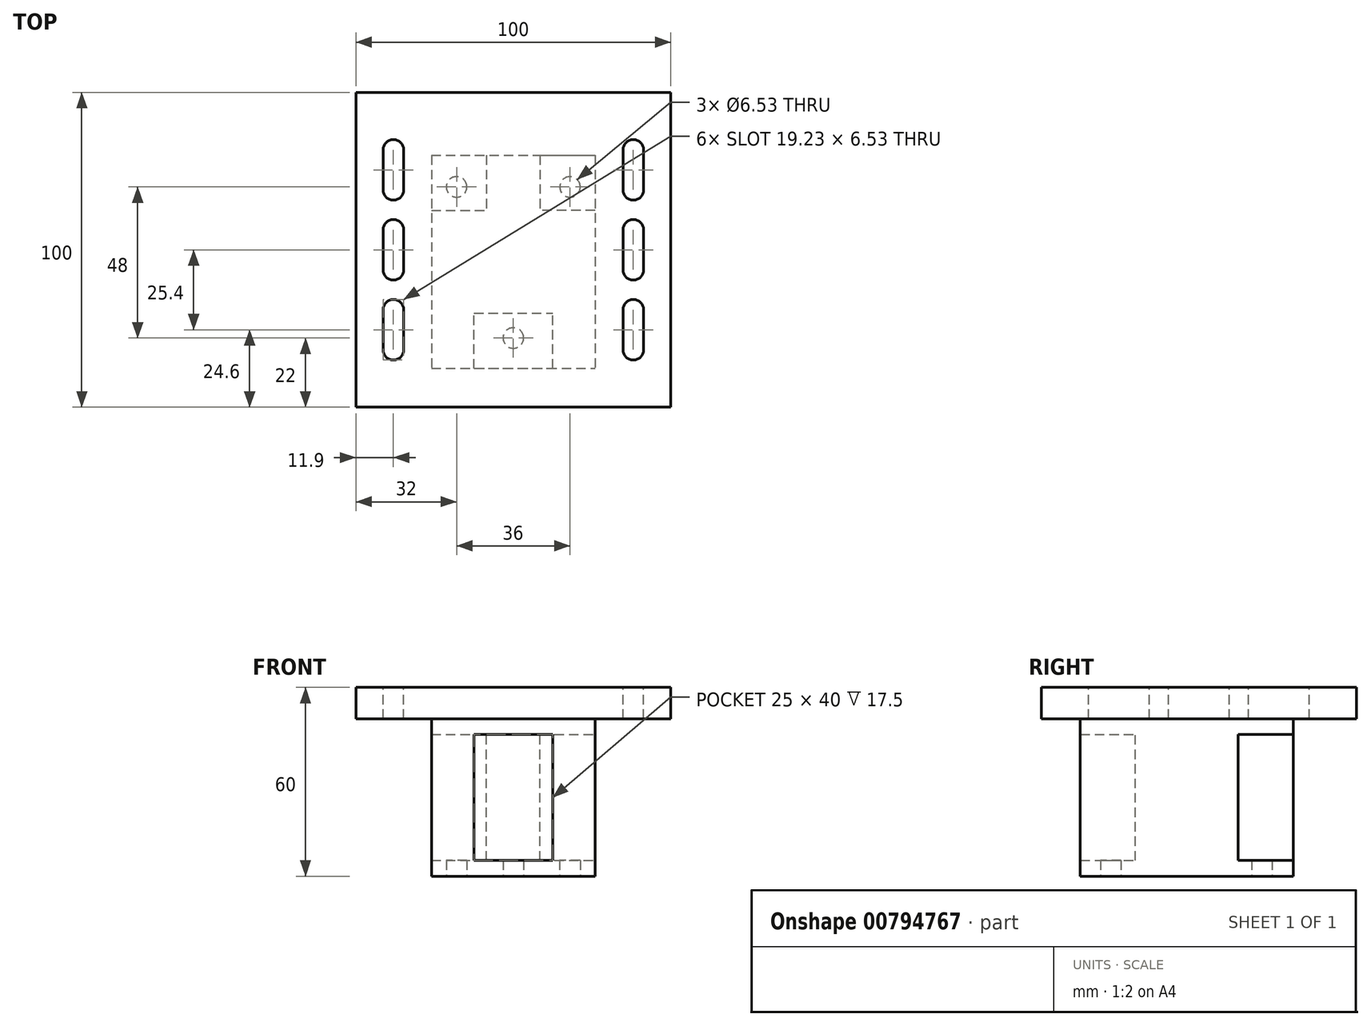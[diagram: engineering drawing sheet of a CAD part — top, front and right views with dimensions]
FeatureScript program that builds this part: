
annotation { "Feature Type Name" : "Feature", "Feature Type Description" : "" }
export const myFeature = defineFeature(function(context is Context, id is Id, definition is map)
    precondition{}
    {
        {
            var Q0;
            Q0=qCreatedBy(makeId("Top.planeOp"),FACE);
            var sketch = newSketch(context, id + "F0", { "sketchPlane" : qUnion([Q0])});
            skLineSegment(sketch, "E0.bottom", {"start": v(-26, 30) * mm, "end": v(26, 30) * mm});
            skLineSegment(sketch, "E0.top", {"start": v(-26, -37.66) * mm, "end": v(26, -37.66) * mm});
            skLineSegment(sketch, "E0.left", {"start": v(-26, 30) * mm, "end": v(-26, -37.66) * mm});
            skLineSegment(sketch, "E0.right", {"start": v(26, 30) * mm, "end": v(26, -37.66) * mm});
            skSolve(sketch);
        }
        {
            var Q0;
            Q0=makeQuery(id+"F0.imprint","IMPRINT",FACE,{"disambiguationData":[TD([[makeQuery(id+"F0.imprint","IMPRINT",EDGE,{"derivedFrom":sQuery(id+"F0.wireOp",EDGE,"E0.bottom")}),-1.0]])]});
            var sketch = newSketch(context, id + "F1", { "sketchPlane" : qUnion([Q0])});
            skCircle(sketch, "E1", {"center": v(-18, 20) * mm, "radius": 3.27 * mm});
            skCircle(sketch, "E2", {"center": v(18, 20) * mm, "radius": 3.27 * mm});
            skCircle(sketch, "E3", {"center": v(0, -28) * mm, "radius": 3.27 * mm});
            skSolve(sketch);
        }
        {
            var Q0;
            Q0=qSketchRegion(id+"F0",true);
            extrude(context, id + "F2", {"entities" : qUnion([Q0]), "depth" : 5 * mm, "offsetDistance" : 25 * mm});
        }
        {
            var Q0;
            Q0=qSketchRegion(id+"F1",true);
            extrude(context, id + "F3", {"entities" : qUnion([Q0]), "operationType" : NewBodyOperationType.REMOVE, "oppositeDirection" : true, "depth" : -5 * mm, "offsetDistance" : 25 * mm});
        }
        {
            var Q0;
            Q0=makeQuery(id+"F2.opExtrude","CAP_FACE",FACE,{"disambiguationData":[OSD([sQuery(id+"F0.wireOp",EDGE,"E0.bottom"),sQuery(id+"F0.wireOp",EDGE,"E0.top"),sQuery(id+"F0.wireOp",EDGE,"E0.left"),sQuery(id+"F0.wireOp",EDGE,"E0.right")])],"isStart":false});
            var sketch = newSketch(context, id + "F4", { "sketchPlane" : qUnion([Q0])});
            skLineSegment(sketch, "E4.bottom", {"start": v(-26, 30) * mm, "end": v(26, 30) * mm});
            skLineSegment(sketch, "E4.top", {"start": v(-26, -37.66) * mm, "end": v(26, -37.66) * mm});
            skLineSegment(sketch, "E4.left", {"start": v(-26, 30) * mm, "end": v(-26, -37.66) * mm});
            skLineSegment(sketch, "E4.right", {"start": v(26, 30) * mm, "end": v(26, -37.66) * mm});
            skSolve(sketch);
        }
        {
            var Q0;
            Q0=qSketchRegion(id+"F4",true);
            extrude(context, id + "F5", {"entities" : qUnion([Q0]), "operationType" : NewBodyOperationType.ADD, "depth" : 30 * mm, "offsetDistance" : 25 * mm});
        }
        {
            var Q0;
            Q0=makeQuery(id+"F5.opExtrude","CAP_FACE",FACE,{"disambiguationData":[OSD([sQuery(id+"F4.wireOp",EDGE,"E4.bottom"),sQuery(id+"F4.wireOp",EDGE,"E4.top"),sQuery(id+"F4.wireOp",EDGE,"E4.left"),sQuery(id+"F4.wireOp",EDGE,"E4.right")])],"isStart":false});
            var sketch = newSketch(context, id + "F6", { "sketchPlane" : qUnion([Q0])});
            skLineSegment(sketch, "E5.bottom", {"start": v(-26, 30) * mm, "end": v(-8.5, 30) * mm});
            skLineSegment(sketch, "E5.top", {"start": v(-26, 12.5) * mm, "end": v(-8.5, 12.5) * mm});
            skLineSegment(sketch, "E5.left", {"start": v(-26, 30) * mm, "end": v(-26, 12.5) * mm});
            skLineSegment(sketch, "E5.right", {"start": v(-8.5, 30) * mm, "end": v(-8.5, 12.5) * mm});
            skLineSegment(sketch, "E6.bottom", {"start": v(26, 30) * mm, "end": v(8.5, 30) * mm});
            skLineSegment(sketch, "E6.top", {"start": v(26, 12.5) * mm, "end": v(8.5, 12.5) * mm});
            skLineSegment(sketch, "E6.left", {"start": v(26, 30) * mm, "end": v(26, 12.5) * mm});
            skLineSegment(sketch, "E6.right", {"start": v(8.5, 30) * mm, "end": v(8.5, 12.5) * mm});
            skLineSegment(sketch, "E7.bottom", {"start": v(-12.5, -37.66) * mm, "end": v(12.5, -37.66) * mm});
            skLineSegment(sketch, "E7.top", {"start": v(-12.5, -20.16) * mm, "end": v(12.5, -20.16) * mm});
            skLineSegment(sketch, "E7.left", {"start": v(-12.5, -37.66) * mm, "end": v(-12.5, -20.16) * mm});
            skLineSegment(sketch, "E7.right", {"start": v(12.5, -37.66) * mm, "end": v(12.5, -20.16) * mm});
            skSolve(sketch);
        }
        {
            var Q0;
            Q0=makeQuery(id+"F5.opExtrude","CAP_FACE",FACE,{"disambiguationData":[OSD([sQuery(id+"F4.wireOp",EDGE,"E4.bottom"),sQuery(id+"F4.wireOp",EDGE,"E4.top"),sQuery(id+"F4.wireOp",EDGE,"E4.left"),sQuery(id+"F4.wireOp",EDGE,"E4.right")])],"isStart":false});
            var sketch = newSketch(context, id + "F7", { "sketchPlane" : qUnion([Q0])});
            skLineSegment(sketch, "E8.bottom", {"start": v(-26, -37.66) * mm, "end": v(26, -37.66) * mm});
            skLineSegment(sketch, "E8.top", {"start": v(-26, 30) * mm, "end": v(26, 30) * mm});
            skLineSegment(sketch, "E8.left", {"start": v(-26, -37.66) * mm, "end": v(-26, 30) * mm});
            skLineSegment(sketch, "E8.right", {"start": v(26, -37.66) * mm, "end": v(26, 30) * mm});
            skSolve(sketch);
        }
        {
            var Q0;
            Q0=qSketchRegion(id+"F7",true);
            extrude(context, id + "F8", {"entities" : qUnion([Q0]), "operationType" : NewBodyOperationType.ADD, "depth" : 25 * mm, "offsetDistance" : 25 * mm});
        }
        {
            var Q0;
            Q0=makeQuery(id+"F8.opExtrude","CAP_FACE",FACE,{"disambiguationData":[OSD([sQuery(id+"F7.wireOp",EDGE,"E8.bottom"),sQuery(id+"F7.wireOp",EDGE,"E8.top"),sQuery(id+"F7.wireOp",EDGE,"E8.left"),sQuery(id+"F7.wireOp",EDGE,"E8.right")])],"isStart":false});
            var sketch = newSketch(context, id + "F9", { "sketchPlane" : qUnion([Q0])});
            skLineSegment(sketch, "E9.bottom", {"start": v(50, -50) * mm, "end": v(-50, -50) * mm});
            skLineSegment(sketch, "E9.top", {"start": v(50, 50) * mm, "end": v(-50, 50) * mm});
            skLineSegment(sketch, "E9.left", {"start": v(50, -50) * mm, "end": v(50, 50) * mm});
            skLineSegment(sketch, "E9.right", {"start": v(-50, -50) * mm, "end": v(-50, 50) * mm});
            skPoint(sketch, "E9.middle", {"position": v(0, 0) * mm});
            skSolve(sketch);
        }
        {
            var Q0;
            Q0=qSketchRegion(id+"F9",true);
            extrude(context, id + "F10", {"entities" : qUnion([Q0]), "operationType" : NewBodyOperationType.ADD, "oppositeDirection" : true, "depth" : 10 * mm, "offsetDistance" : 25 * mm});
        }
        {
            var Q0;
            Q0=makeQuery(id+"F10.boolean.opBoolean","MERGE",FACE,{"derivedFrom":[makeQuery(id+"F8.opExtrude","CAP_FACE",FACE,{"disambiguationData":[OSD([sQuery(id+"F7.wireOp",EDGE,"E8.bottom"),sQuery(id+"F7.wireOp",EDGE,"E8.top"),sQuery(id+"F7.wireOp",EDGE,"E8.left"),sQuery(id+"F7.wireOp",EDGE,"E8.right")])],"isStart":false}),makeQuery(id+"F10.opExtrude","CAP_FACE",FACE,{"disambiguationData":[OSD([sQuery(id+"F9.wireOp",EDGE,"E9.bottom"),sQuery(id+"F9.wireOp",EDGE,"E9.top"),sQuery(id+"F9.wireOp",EDGE,"E9.left"),sQuery(id+"F9.wireOp",EDGE,"E9.right")])],"isStart":true})]});
            var sketch = newSketch(context, id + "F11", { "sketchPlane" : qUnion([Q0])});
            skCircle(sketch, "E10", {"center": v(38.1, -6.35) * mm, "radius": 3.27 * mm});
            skCircle(sketch, "E11", {"center": v(38.1, 6.35) * mm, "radius": 3.27 * mm});
            skLineSegment(sketch, "E12.bottom", {"start": v(34.84, 6.35) * mm, "end": v(41.37, 6.35) * mm});
            skLineSegment(sketch, "E12.top", {"start": v(34.84, -6.35) * mm, "end": v(41.37, -6.35) * mm});
            skLineSegment(sketch, "E12.left", {"start": v(34.84, 6.35) * mm, "end": v(34.84, -6.35) * mm});
            skLineSegment(sketch, "E12.right", {"start": v(41.37, 6.35) * mm, "end": v(41.37, -6.35) * mm});
            skCircle(sketch, "E13", {"center": v(38.1, -31.75) * mm, "radius": 3.27 * mm});
            skCircle(sketch, "E14", {"center": v(38.1, -19.05) * mm, "radius": 3.27 * mm});
            skLineSegment(sketch, "E15.bottom", {"start": v(34.84, -19.05) * mm, "end": v(41.37, -19.05) * mm});
            skLineSegment(sketch, "E15.top", {"start": v(34.84, -31.75) * mm, "end": v(41.37, -31.75) * mm});
            skLineSegment(sketch, "E15.left", {"start": v(34.84, -19.05) * mm, "end": v(34.84, -31.75) * mm});
            skLineSegment(sketch, "E15.right", {"start": v(41.37, -19.05) * mm, "end": v(41.37, -31.75) * mm});
            skCircle(sketch, "E16.MirrorC", {"center": v(38.1, 31.75) * mm, "radius": 3.27 * mm});
            skLineSegment(sketch, "E17.MirrorCS", {"start": v(41.37, 19.05) * mm, "end": v(41.37, 31.75) * mm});
            skLineSegment(sketch, "E18.MirrorCS", {"start": v(34.84, 19.05) * mm, "end": v(34.84, 31.75) * mm});
            skCircle(sketch, "E19.MirrorC", {"center": v(38.1, 19.05) * mm, "radius": 3.27 * mm});
            skCircle(sketch, "E20.MirrorC", {"center": v(-38.1, -31.75) * mm, "radius": 3.27 * mm});
            skLineSegment(sketch, "E21.MirrorCS", {"start": v(-41.37, -19.05) * mm, "end": v(-41.37, -31.75) * mm});
            skLineSegment(sketch, "E22.MirrorCS", {"start": v(-34.84, -19.05) * mm, "end": v(-34.84, -31.75) * mm});
            skCircle(sketch, "E23.MirrorC", {"center": v(-38.1, -19.05) * mm, "radius": 3.27 * mm});
            skCircle(sketch, "E24.MirrorC", {"center": v(-38.1, -6.35) * mm, "radius": 3.27 * mm});
            skLineSegment(sketch, "E25.MirrorCS", {"start": v(-41.37, 6.35) * mm, "end": v(-41.37, -6.35) * mm});
            skLineSegment(sketch, "E26.MirrorCS", {"start": v(-34.84, 6.35) * mm, "end": v(-34.84, -6.35) * mm});
            skCircle(sketch, "E27.MirrorC", {"center": v(-38.1, 6.35) * mm, "radius": 3.27 * mm});
            skCircle(sketch, "E28.MirrorC", {"center": v(-38.1, 19.05) * mm, "radius": 3.27 * mm});
            skLineSegment(sketch, "E29.MirrorCS", {"start": v(-34.84, 19.05) * mm, "end": v(-34.84, 31.75) * mm});
            skLineSegment(sketch, "E30.MirrorCS", {"start": v(-41.37, 19.05) * mm, "end": v(-41.37, 31.75) * mm});
            skCircle(sketch, "E31.MirrorC", {"center": v(-38.1, 31.75) * mm, "radius": 3.27 * mm});
            skSolve(sketch);
        }
        {
            var Q0;
            Q0=qSketchRegion(id+"F11",true);
            extrude(context, id + "F12", {"entities" : qUnion([Q0]), "operationType" : NewBodyOperationType.REMOVE, "oppositeDirection" : true, "depth" : 10 * mm, "offsetDistance" : 25 * mm});
        }
        {
            var Q0;
            Q0=qSketchRegion(id+"F6",true);
            extrude(context, id + "F13", {"entities" : qUnion([Q0]), "operationType" : NewBodyOperationType.REMOVE, "oppositeDirection" : true, "depth" : 30 * mm, "offsetDistance" : 25 * mm, "hasSecondDirection" : true, "secondDirectionOppositeDirection" : false, "secondDirectionDepth" : 10 * mm});
        }
    });
